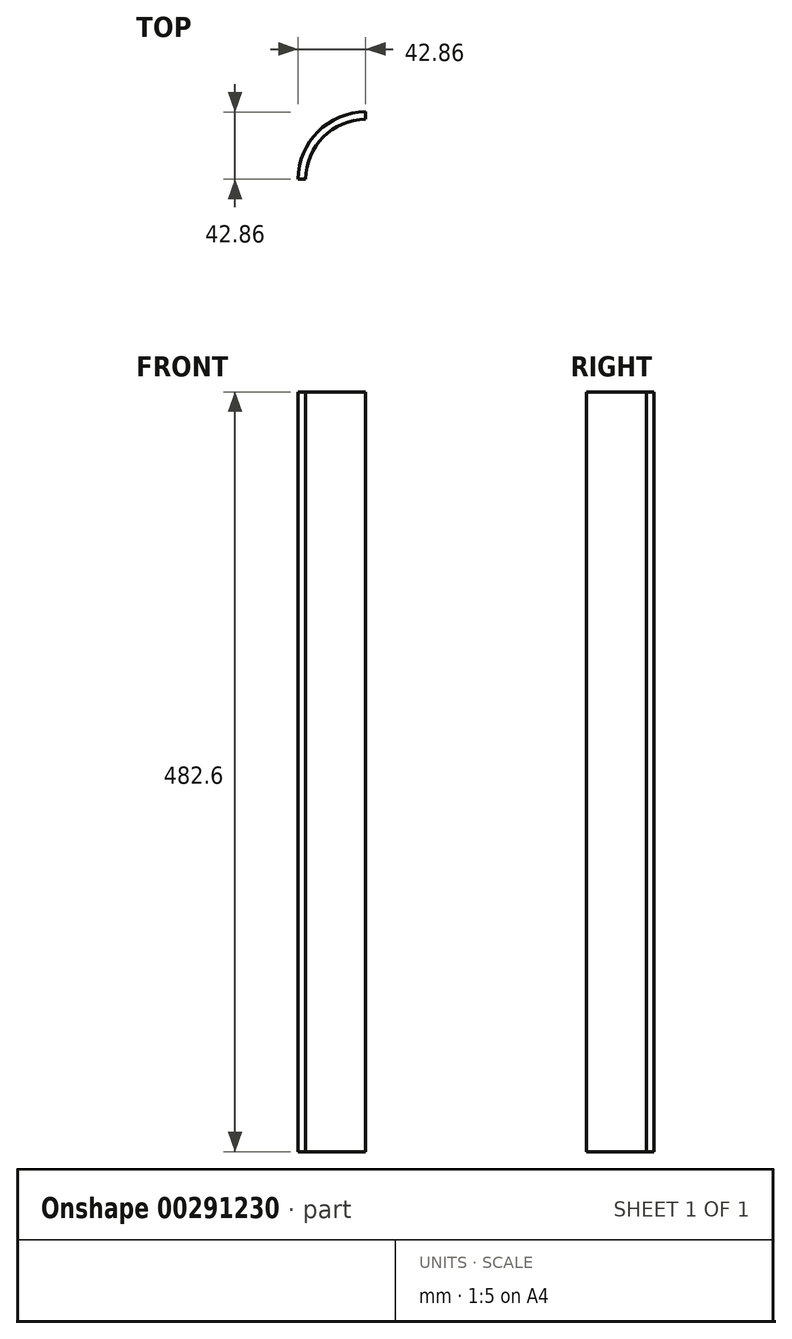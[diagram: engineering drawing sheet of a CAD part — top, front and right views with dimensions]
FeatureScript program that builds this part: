
annotation { "Feature Type Name" : "Feature", "Feature Type Description" : "" }
export const myFeature = defineFeature(function(context is Context, id is Id, definition is map)
    precondition{}
    {
        {
            var Q0;
            Q0=qCreatedBy(makeId("Top.planeOp"),FACE);
            var sketch = newSketch(context, id + "F0", { "sketchPlane" : qUnion([Q0])});
            skArc(sketch, "E0", {"start": v(0, 38.1) * mm, "mid": v(-26.94, 26.94) * mm, "end": v(-38.1, 0) * mm});
            skArc(sketch, "E1", {"start": v(0, 42.86) * mm, "mid": v(-30.3, 30.3) * mm, "end": v(-42.86, 0) * mm});
            skLineSegment(sketch, "E2", {"start": v(-42.86, 0) * mm, "end": v(-38.1, 0) * mm});
            skLineSegment(sketch, "E3", {"start": v(0, 42.86) * mm, "end": v(0, 38.1) * mm});
            skPoint(sketch, "E4.orphan", {"position": v(-69.94, 0) * mm});
            skPoint(sketch, "E5.orphan", {"position": v(0, 55.55) * mm});
            skSolve(sketch);
        }
        {
            var Q0;
            Q0=makeQuery(id+"F0.imprint","IMPRINT",FACE,{"disambiguationData":[TD([[makeQuery(id+"F0.imprint","IMPRINT",EDGE,{"derivedFrom":sQuery(id+"F0.wireOp",EDGE,"E0")}),-1.0]])]});
            extrude(context, id + "F1", {"entities" : qUnion([Q0]), "depth" : 482.6 * mm});
        }
    });
